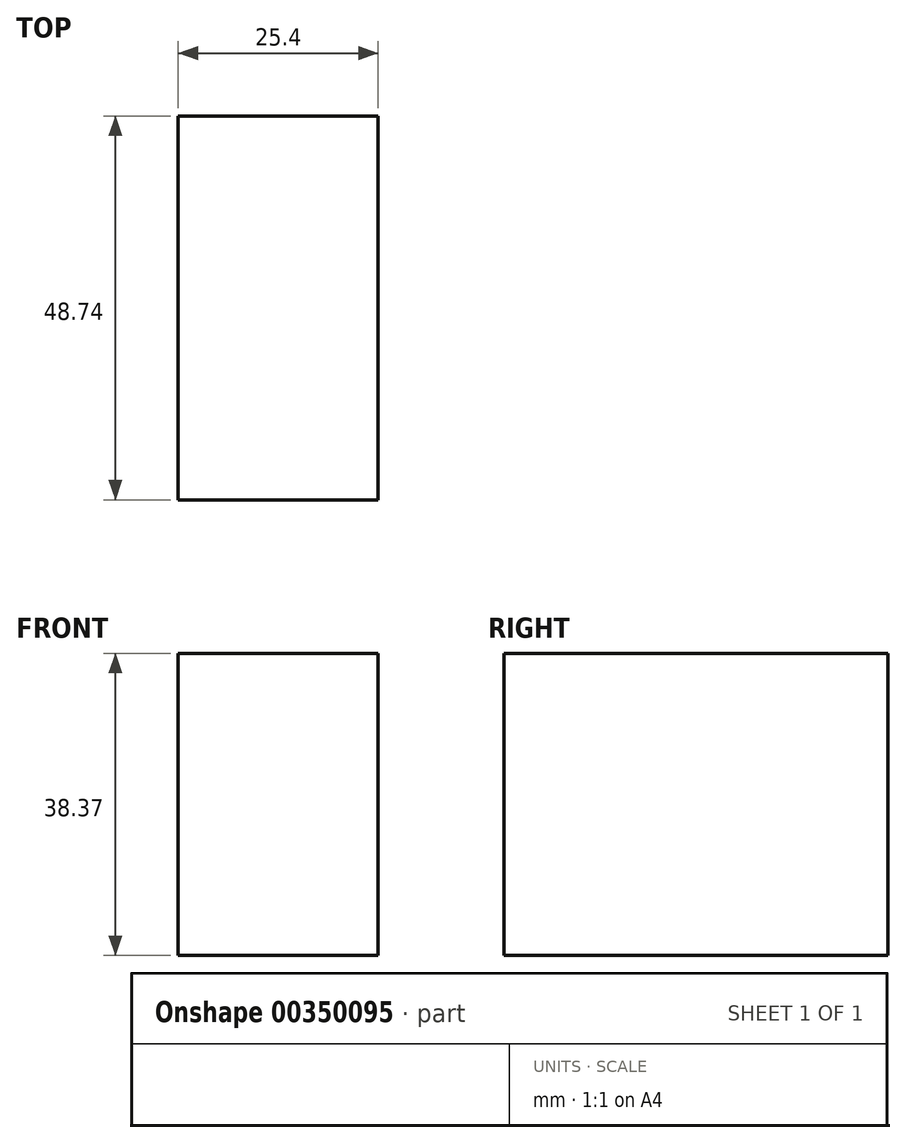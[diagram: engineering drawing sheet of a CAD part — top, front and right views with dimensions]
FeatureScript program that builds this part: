
annotation { "Feature Type Name" : "Feature", "Feature Type Description" : "" }
export const myFeature = defineFeature(function(context is Context, id is Id, definition is map)
    precondition{}
    {
        {
            var Q0;
            Q0=qCreatedBy(makeId("Right.planeOp"),FACE);
            var sketch = newSketch(context, id + "F0", { "sketchPlane" : qUnion([Q0])});
            skLineSegment(sketch, "E0.bottom", {"start": v(-56, 38.37) * mm, "end": v(-7.26, 38.37) * mm});
            skLineSegment(sketch, "E0.top", {"start": v(-56, 0) * mm, "end": v(-7.26, 0) * mm});
            skLineSegment(sketch, "E0.left", {"start": v(-56, 38.37) * mm, "end": v(-56, 0) * mm});
            skLineSegment(sketch, "E0.right", {"start": v(-7.26, 38.37) * mm, "end": v(-7.26, 0) * mm});
            skSolve(sketch);
        }
        {
            var Q0;
            Q0=makeQuery(id+"F0.imprint","IMPRINT",FACE,{"disambiguationData":[TD([[makeQuery(id+"F0.imprint","IMPRINT",EDGE,{"derivedFrom":sQuery(id+"F0.wireOp",EDGE,"E0.bottom")}),-1.0]])]});
            extrude(context, id + "F1", {"entities" : qUnion([Q0]), "depth" : 25.4 * mm});
        }
    });
